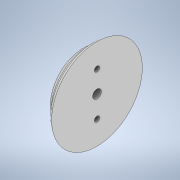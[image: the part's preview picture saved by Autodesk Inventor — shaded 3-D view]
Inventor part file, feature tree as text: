
AUTODESK INVENTOR PART (.ipt)
format: ipt  version: 2022 (Build 260153000, 153)  size: 131,584 bytes
history: native  units: mm
features: sketch x2, revolve x1, extrude x1
ambient origin geometry x8: Origin, YZ Plane, XZ Plane, XY Plane, X Axis, Y Axis, Z Axis, Center Point
bodies: Solid1 (feature_tree)
feature tree (4):
  revolve  "Revolution1"  [1 undecoded]
  extrude  "Extrusion1"  Depth=8.0mm
  sketch  "Sketch1"  dims[d0=18.0mm d1=8.0mm]
  sketch  "Sketch2"  dims[d2=27.0mm d3=8.0mm d4=90.0deg d5=5.0mm d6=12.5mm d7=12.5mm d8=3.0mm d9=3.0mm d10=10.0mm d11=0.0mm]
note: 1 required parameter value undecoded (feature->parameter linkage not recoverable at this tier; creation-order binding heuristic only, values carry confidence <= 0.55)
